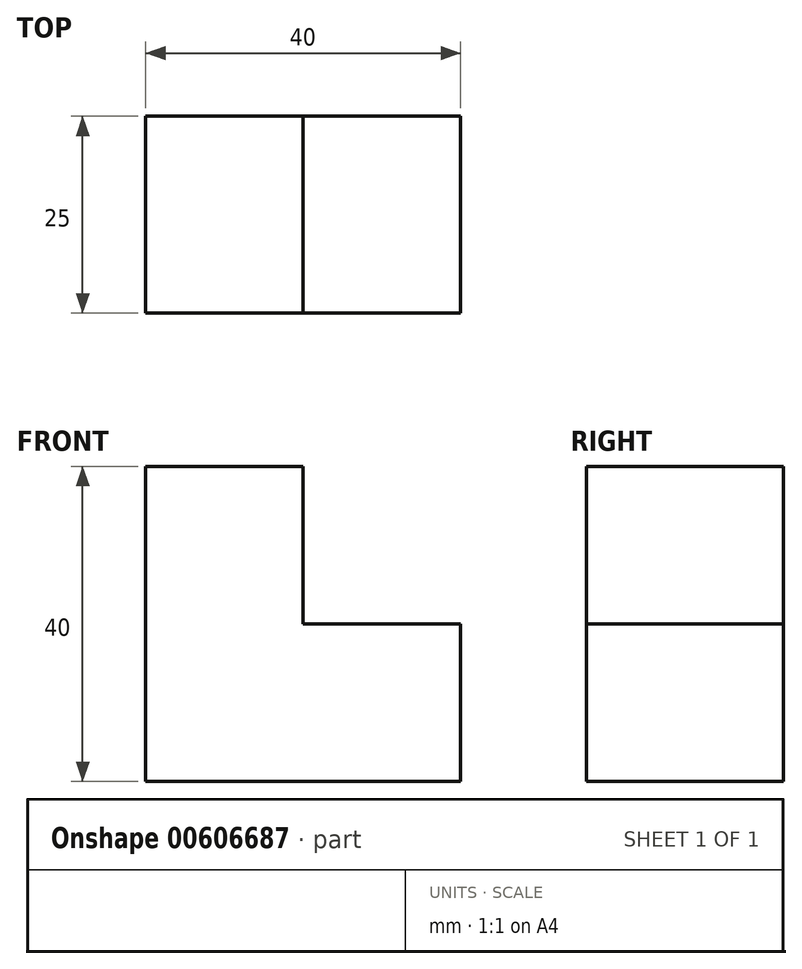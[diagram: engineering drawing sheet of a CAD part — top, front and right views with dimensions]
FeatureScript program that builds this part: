
annotation { "Feature Type Name" : "Feature", "Feature Type Description" : "" }
export const myFeature = defineFeature(function(context is Context, id is Id, definition is map)
    precondition{}
    {
        {
            var Q0;
            Q0=qCreatedBy(makeId("Front.planeOp"),FACE);
            var sketch = newSketch(context, id + "F0", { "sketchPlane" : qUnion([Q0])});
            skLineSegment(sketch, "E0", {"start": v(0, 0) * mm, "end": v(0, 40) * mm});
            skLineSegment(sketch, "E1", {"start": v(0, 40) * mm, "end": v(20, 40) * mm});
            skLineSegment(sketch, "E2", {"start": v(20, 40) * mm, "end": v(20, 20) * mm});
            skLineSegment(sketch, "E3", {"start": v(20, 20) * mm, "end": v(40, 20) * mm});
            skLineSegment(sketch, "E4", {"start": v(40, 20) * mm, "end": v(40, 0) * mm});
            skLineSegment(sketch, "E5", {"start": v(40, 0) * mm, "end": v(0, 0) * mm});
            skSolve(sketch);
        }
        {
            var Q0;
            Q0 = qSketchRegion(id + "F0", true);
            extrude(context, id + "F1", {"entities" : qUnion([Q0]), "depth" : 25 * mm, "offsetDistance" : 25 * mm});
        }
    });
